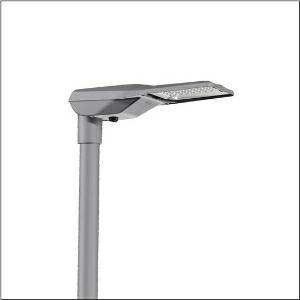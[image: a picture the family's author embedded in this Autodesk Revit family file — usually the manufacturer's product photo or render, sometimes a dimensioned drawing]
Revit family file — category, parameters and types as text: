
# Revit family: streetlight_sl_21_mini___st1_0a_5xe2d33r08gb_66de
name_source: partatom
category: Lighting Fixtures
units: mm (PartAtom-declared; Revit-internal decimal feet)

## family parameters
Cut with Voids When Loaded = No
Host = Face
Light Source = No
Part Type = Normal
Room Calculation Point = No
Round Connector Dimension = Use Diameter
Shared = No

## types (1)
- --- (1 x LED, 5940 lm, 40.4 W, 3000K)
    Apparent Load = 40 VA
    CIE Flux Codes = 37 72 97 100 100
    Color Rendering = 70
    Color Temperature = 3000K
    Default Elevation = 1800 mm
    Description = Streetlight SL 21 mini, mast luminaire, primary light control with lens, of PMMA, primary optical cover: cover, of toughened safety glass, transparent, light distribution: ST1.0a, light emission: direct distribution, primary light characteristic: asymmetric, installation type: side-entry, post-top, LED, High Power LED, rated luminous flux: 5.940lm, luminous efficacy: 147lm/W, light colour: 730, colour temperature: 3000K, control gear: D4i, control: flexible luminous flux parameterisation, time-dependent luminous flux control, constant luminous flux control, overheat protection, pre-setting: logarithmic dimming characteristic, mains connection: 220..240V, AC, 50/60Hz, start of lifetime: 40W, end of service life: 41W, reduction: 19W, luminaire housing, of diecast aluminium, powder-coated, Siteco® metallic grey (DB 702S), corrosivity category C5 mid according to DIN EN ISO 12944, please order mast flange separately, inclination adjustable: 0°, 5°, 10°, 15°, sealing non-destructively replaceable, multi-level sealing system, length: 628mm, width: 235mm, height: 110mm, mast flange for spigot size: 42mm (side-entry): 5XC10008XM4, 60/48mm (side-entry/post-top): 5XC10108XM2, 76/60mm (side-entry/post-top): 5XC10108XM1, mounting height: 4..8m, Smart Interface below, protection rating (complete): IP66, insulation class (complete): insulation class II (safety insulation), certification: CE, ENEC, ENEC+, VDE, impact resistance: IK10, permissible operating ambient temperature for outdoor applications: -40..+50°C, standard-compliant lighting for roads and squares, packaging unit: 1 piece

Light Distribution: ST1.0a
    Height = 110 mm
    Lamp = 1 x LED
    Lamp Light Flux = 5940 lm
    Lamp Power = 40.4 W
    Lamp count = 1
    Length = 625 mm
    Luminous efficacy = 147 lm/W
    Manufacturer = Siteco
    ModVariant = No
    Model = 5XE2D33R08GB
    Number of Poles = 1
    OnlyDefault = Yes
    Power Factor = 1
    Product Name = Streetlight SL 21 mini | ST1.0a
    Product group = mast luminaire | pylon top
    ProductGroupID = 6100
    Protection Class = Protection class II
    Protection Degree = IP 66
    RLX_Detail_Level = 1
    RLX_Emergency_Light_Flux = 0 lm
    RLX_Emergency_Type = 0
    RLX_Emergency_Type_DB = No
    RlxData = <blob elided: 26225 chars, md5=9753e79d>
    Socket = socket
    Standby Power = 0 W
    System Light Flux = 5940 lm
    System Power = 40 W
    Type Comments = factory setting: luminous flux: 100 % | dim-lin: 254 | 812 mA
    Type Image = l_1003516.jpg
    URL = http://relux.com
    VarID = @adj_210103
    Voltage = 0 V
    Weight = 0.00 kg
    Width = 234 mm

## geometry (parser evidence)
native form markers: Blend x4, Sweep x12
no freeform markers — native parametric forms only
